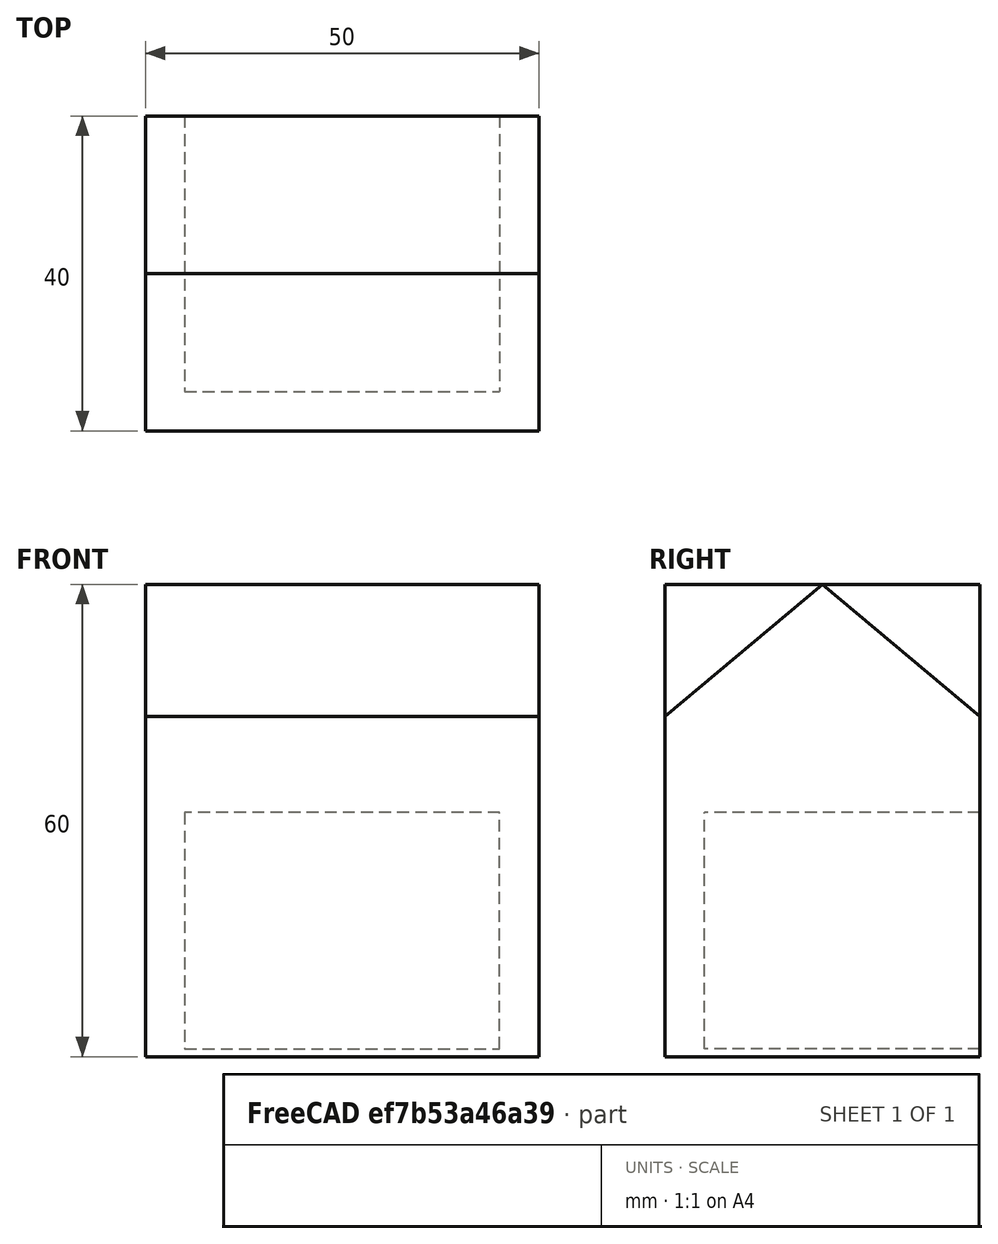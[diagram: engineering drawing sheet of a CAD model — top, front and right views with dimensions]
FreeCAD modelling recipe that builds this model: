
FCSTD DOCUMENT  (FreeCAD 0.16R)
Label: Tuxyhouse
License: All rights reserved
LicenseURL: http://en.wikipedia.org/wiki/All_rights_reserved
objects: Sketcher::SketchObject×3, PartDesign::Pocket×2, PartDesign::Pad×1, PartDesign::Mirrored×1, Part::FeaturePython×1, Mesh::Feature×1
note: 11 computed .brp shape members not serialized (recipe doc carries the construction recipe); baked Part::Feature solids carry a one-line shape summary decoded from their .brp

FEATURE [Sketcher::SketchObject] Sketch
  sketch-geometry (4):
    g0: LineSegment StartX=-25 StartY=20 StartZ=0 EndX=25 EndY=20 EndZ=0
    g1: LineSegment StartX=25 StartY=20 StartZ=0 EndX=25 EndY=-20 EndZ=0
    g2: LineSegment StartX=25 StartY=-20 StartZ=0 EndX=-25 EndY=-20 EndZ=0
    g3: LineSegment StartX=-25 StartY=-20 StartZ=0 EndX=-25 EndY=20 EndZ=0
  constraints (12):
    c: Coincident(g0,g1)
    c: Coincident(g1,g2)
    c: Coincident(g2,g3)
    c: Coincident(g3,g0)
    c: Horizontal(g0)
    c: Horizontal(g2)
    c: Vertical(g1)
    c: Vertical(g3)
    c: DistanceY(g1,g1) = 40
    c: DistanceX(g0,g0) = 50
    c: Symmetric(g2,g1,g-2)
    c: Symmetric(g0,g2,g-1)
FEATURE [PartDesign::Pad] Pad
  Length = 60
  Length2 = 100
  Sketch = -> Sketch
  Type = 0
FEATURE [Sketcher::SketchObject] Sketch001
  ExternalGeometry = -> [Pad]
  Placement = pos=(25,0,0) rot=(0.57735,0.57735,0.57735;2.0944rad)
  Support = -> Pad [Face2]
  sketch-geometry (4):
    g0: LineSegment StartX=36.6937 StartY=29.2103 StartZ=0 EndX=45.0115 EndY=76.3828 EndZ=0
    g1: LineSegment StartX=45.0115 StartY=76.3828 StartZ=0 EndX=0 EndY=60 EndZ=0
    g2: LineSegment StartX=0 StartY=60 StartZ=0 EndX=36.6937 EndY=29.2103 EndZ=0
    g3: Circle [constr] CenterX=27.235 CenterY=55.1977 CenterZ=0 NormalX=0 NormalY=0 NormalZ=1 Radius=27.6552
  constraints (12):
    c: Coincident(g0,g1)
    c: Coincident(g1,g2)
    c: Coincident(g2,g0)
    c: Equal(g0,g1)
    c: Equal(g0,g2)
    c: PointOnObject(g0,g3)
    c: PointOnObject(g1,g3)
    c: PointOnObject(g2,g3)
    c: PointOnObject(g1,g-2)
    c: DistanceY(g-3,g1) = 0
    c: Distance(g1) = 47.9002
    c: Angle(g2) = -0.698132
FEATURE [PartDesign::Pocket] Pocket
  Length = 5
  Sketch = -> Sketch001
  Type = 1
FEATURE [PartDesign::Mirrored] Mirrored
  MirrorPlane = -> Sketch001 [V_Axis]
  Originals = -> [Pocket]
FEATURE [Sketcher::SketchObject] Sketch002
  Placement = pos=(0,20,0) rot=(0,0.707107,0.707107;3.14159rad)
  Support = -> Mirrored [Face1]
  sketch-geometry (4):
    g0: LineSegment StartX=-20 StartY=31 StartZ=0 EndX=20 EndY=31 EndZ=0
    g1: LineSegment StartX=20 StartY=31 StartZ=0 EndX=20 EndY=1 EndZ=0
    g2: LineSegment StartX=20 StartY=1 StartZ=0 EndX=-20 EndY=1 EndZ=0
    g3: LineSegment StartX=-20 StartY=1 StartZ=0 EndX=-20 EndY=31 EndZ=0
  constraints (12):
    c: Coincident(g0,g1)
    c: Coincident(g1,g2)
    c: Coincident(g2,g3)
    c: Coincident(g3,g0)
    c: Horizontal(g0)
    c: Horizontal(g2)
    c: Vertical(g1)
    c: Vertical(g3)
    c: Symmetric(g0,g0,g-2)
    c: DistanceX(g0,g0) = 40
    c: DistanceY(g1,g1) = 30
    c: DistanceY(g1,g-1) = -1
FEATURE [PartDesign::Pocket] Pocket001
  Length = 35
  Sketch = -> Sketch002
  Type = 0
FEATURE [Part::FeaturePython] refine  label="refine_Pocket001"  # WARN: FeaturePython — macro-defined, semantics opaque (R4)
  Base = -> Pocket001
FEATURE [Mesh::Feature] Mesh  label="refine_Pocket001 (Meshed)"
